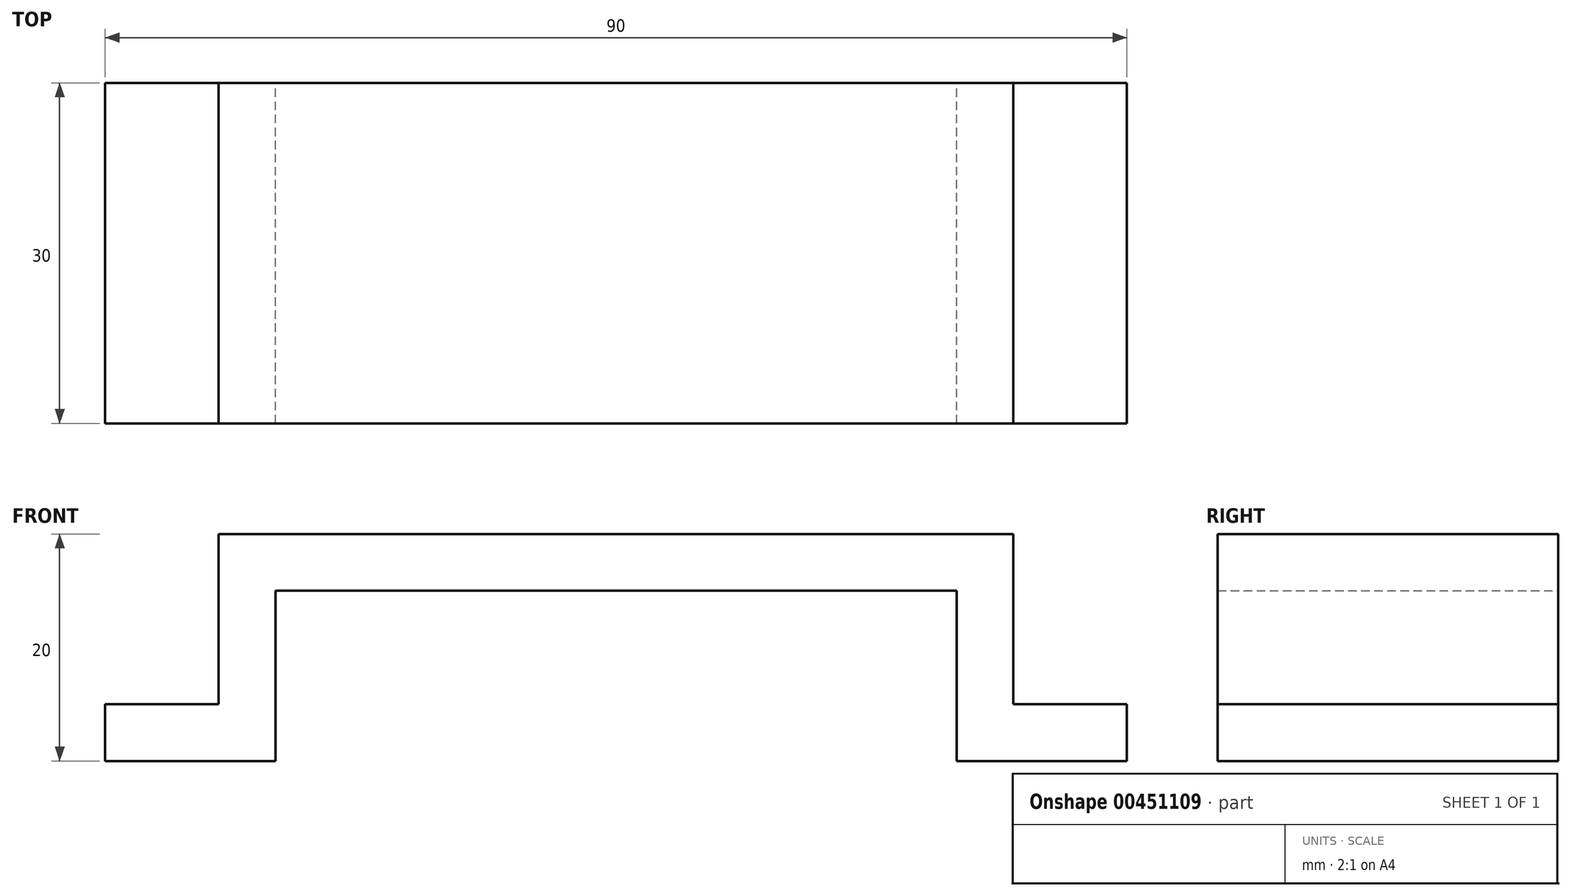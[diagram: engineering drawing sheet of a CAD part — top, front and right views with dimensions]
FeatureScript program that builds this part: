
annotation { "Feature Type Name" : "Feature", "Feature Type Description" : "" }
export const myFeature = defineFeature(function(context is Context, id is Id, definition is map)
    precondition{}
    {
        {
            var Q0;
            Q0=qCreatedBy(makeId("Front.planeOp"),FACE);
            var sketch = newSketch(context, id + "F0", { "sketchPlane" : qUnion([Q0])});
            skLineSegment(sketch, "E0", {"start": v(-45, 5) * mm, "end": v(-45, 0) * mm});
            skLineSegment(sketch, "E1", {"start": v(-45, 0) * mm, "end": v(-30, 0) * mm});
            skLineSegment(sketch, "E2", {"start": v(-45, 5) * mm, "end": v(-35, 5) * mm});
            skLineSegment(sketch, "E3", {"start": v(-35, 5) * mm, "end": v(-35, 20) * mm});
            skLineSegment(sketch, "E4", {"start": v(-35, 20) * mm, "end": v(35, 20) * mm});
            skLineSegment(sketch, "E5", {"start": v(35, 20) * mm, "end": v(35, 5) * mm});
            skLineSegment(sketch, "E6", {"start": v(35, 5) * mm, "end": v(45, 5) * mm});
            skLineSegment(sketch, "E7", {"start": v(45, 5) * mm, "end": v(45, 0) * mm});
            skLineSegment(sketch, "E8", {"start": v(45, 0) * mm, "end": v(30, 0) * mm});
            skLineSegment(sketch, "E9", {"start": v(30, 0) * mm, "end": v(30, 15) * mm});
            skLineSegment(sketch, "E10", {"start": v(30, 15) * mm, "end": v(-30, 15) * mm});
            skLineSegment(sketch, "E11", {"start": v(-30, 15) * mm, "end": v(-30, 0) * mm});
            skSolve(sketch);
        }
        {
            var Q0;
            Q0 = qSketchRegion(id + "F0", true);
            extrude(context, id + "F1", {"entities" : qUnion([Q0]), "depth" : 30 * mm, "offsetDistance" : 25 * mm});
        }
    });
